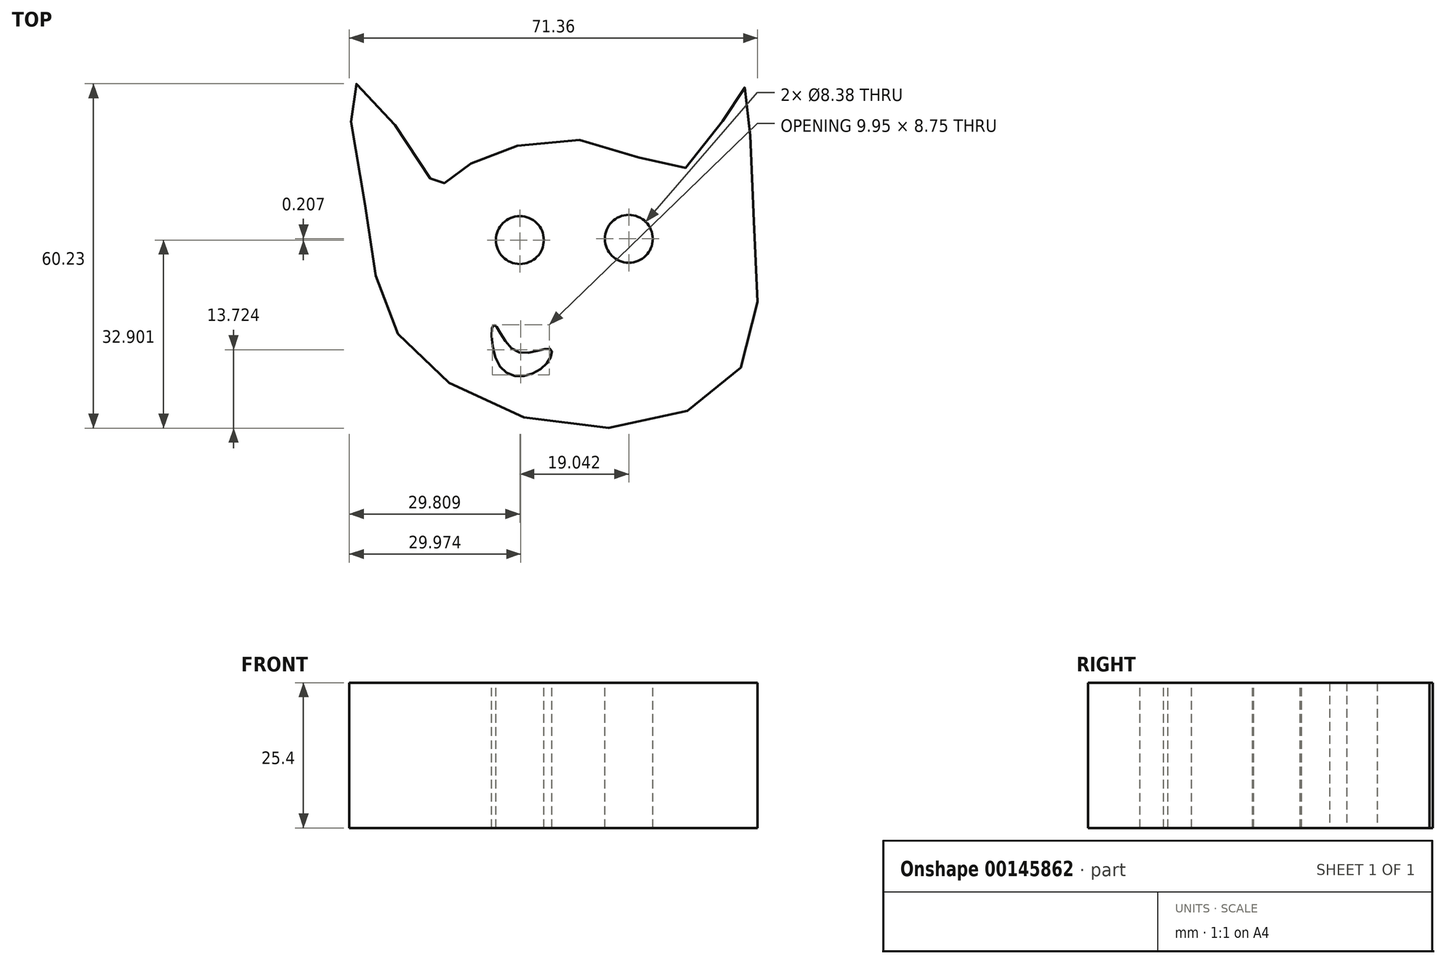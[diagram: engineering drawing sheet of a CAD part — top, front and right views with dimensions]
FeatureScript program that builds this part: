
annotation { "Feature Type Name" : "Feature", "Feature Type Description" : "" }
export const myFeature = defineFeature(function(context is Context, id is Id, definition is map)
    precondition{}
    {
        {
            var Q0;
            Q0=qCreatedBy(makeId("Top.planeOp"),FACE);
            var sketch = newSketch(context, id + "F0", { "sketchPlane" : qUnion([Q0])});
            skFitSpline(sketch, "E0", {"points": [v(-42.85, 21.22) * mm, v(-44.5, 42.13) * mm, v(-31.88, 26.4) * mm, v(-30.02, 24.12) * mm, v(-27.74, 25.77) * mm, v(-20.08, 30.12) * mm, v(0, 31.36) * mm, v(14.08, 27.84) * mm, v(23.19, 41.5) * mm, v(24.84, 23.08) * mm, v(22.56, -7.97) * mm, v(-6.21, -17.9) * mm, v(-36.23, -2.8) * mm, v(-42.85, 21.22) * mm]});
            skSolve(sketch);
        }
        {
            var Q0;
            Q0 = qSketchRegion(id + "F0", true);
            extrude(context, id + "F1", {"entities" : qUnion([Q0]), "depth" : 25.4 * mm});
        }
        {
            var Q0;
            Q0=makeQuery(id+"F1.opExtrude","CAP_FACE",FACE,{"disambiguationData":[OSD([sQuery(id+"F0.wireOp",EDGE,"E0")])],"isStart":false});
            var sketch = newSketch(context, id + "F2", { "sketchPlane" : qUnion([Q0])});
            skCircle(sketch, "E1", {"center": v(-15.73, 14.8) * mm, "radius": 4.2 * mm});
            skCircle(sketch, "E2", {"center": v(3.31, 15) * mm, "radius": 4.2 * mm});
            skFitSpline(sketch, "E3", {"points": [v(-20.29, 0) * mm, v(-16.35, -4.66) * mm, v(-10.35, -4.24) * mm, v(-11.8, -7.56) * mm, v(-19.05, -7.56) * mm, v(-20.29, 0) * mm]});
            skSolve(sketch);
        }
        {
            var Q0;
            Q0 = qSketchRegion(id + "F2", true);
            extrude(context, id + "F3", {"entities" : qUnion([Q0]), "operationType" : NewBodyOperationType.REMOVE, "oppositeDirection" : true, "depth" : 25.4 * mm});
        }
    });
